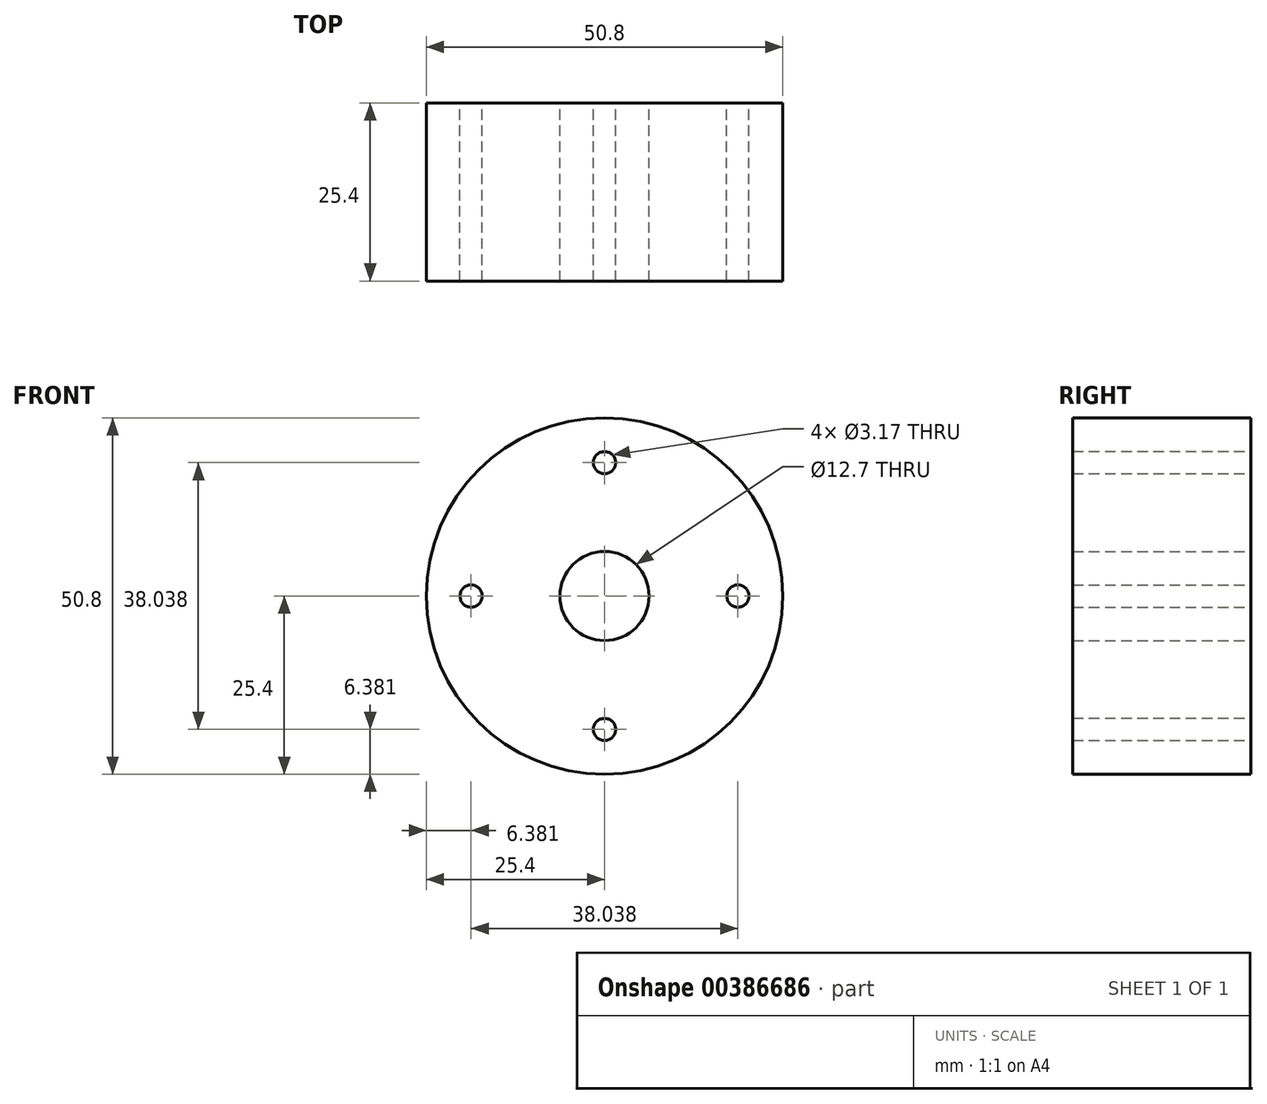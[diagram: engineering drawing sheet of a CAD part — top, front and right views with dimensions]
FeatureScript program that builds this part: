
annotation { "Feature Type Name" : "Feature", "Feature Type Description" : "" }
export const myFeature = defineFeature(function(context is Context, id is Id, definition is map)
    precondition{}
    {
        {
            var Q0;
            Q0=qCreatedBy(makeId("Front.planeOp"),FACE);
            var sketch = newSketch(context, id + "F0", { "sketchPlane" : qUnion([Q0])});
            skCircle(sketch, "E0", {"center": v(0, 0) * mm, "radius": 25.4 * mm});
            skCircle(sketch, "E1", {"center": v(0, 0) * mm, "radius": 22.23 * mm, "construction": true});
            skCircle(sketch, "E2", {"center": v(0, 0) * mm, "radius": 6.35 * mm});
            skCircle(sketch, "E3", {"center": v(0, 19.02) * mm, "radius": 1.59 * mm});
            skCircle(sketch, "E4.1.0", {"center": v(-19.02, 0) * mm, "radius": 1.59 * mm});
            skCircle(sketch, "E4.2.0", {"center": v(0, -19.02) * mm, "radius": 1.59 * mm});
            skCircle(sketch, "E4.3.0", {"center": v(19.02, 0) * mm, "radius": 1.59 * mm});
            skSolve(sketch);
        }
        {
            var Q0;
            Q0 = qSketchRegion(id + "F0", true);
            extrude(context, id + "F1", {"entities" : qUnion([Q0]), "depth" : 25.4 * mm});
        }
    });
